# Revit family: APL Residential Thermal Heart Hinged Door Open In
name_source: partatom
category: Doors
revit_build: Autodesk Revit LT 2017 (Build: 20160225_1515(x64)
units: mm (PartAtom-declared; Revit-internal decimal feet)

## family parameters
Always vertical = Yes
Cut with Voids When Loaded = No
Host = Wall
OmniClass Number = 23.30.10.00
OmniClass Title = Doors
Room Calculation Point = No
Shared = No

## types (2) — shared parameters
Analytic Construction = <None>
Frame Projection Int. = 20 mm  [stored 0.0656168 ft]
Frame Width Sill = 15 mm  [stored 0.0492126 ft]
Function = Interior
Groove = 10 mm  [stored 0.0328084 ft]
Height = 2303 mm
Jamb Liner 1 = Yes
Jamb Liner 2 = Yes
Liner End = 10 mm  [stored 0.0328084 ft]
Liner Head = Yes
Liner Sill = No
Panel = 720 mm  [stored 2.3622 ft]
Plan Swing = Yes
Rough Height = 2315 mm  [stored 7.59514 ft]
Rough Width = 815 mm
Wall Closure = By host
Width = 800 mm  [stored 2.62467 ft]

## per-type parameters (varying)
| type | Frame Projection Ext. | Frame Width | Liner | Reveal Liner |
| Architrave | 13 mm | 12 mm  [stored 0.0393701 ft] | 51 mm | No |
| Liner | 14 mm  [stored 0.0459318 ft] | 13 mm | 407 mm | Yes |

type visibility flags (boolean, named after types; folded from table):
- Architrave: Yes: Architrave
- Liner: Yes: (none)

note: [stored X ft] marks values corroborated as IEEE doubles in the binary element streams (Revit-internal decimal feet)

## geometry (parser evidence)
native form markers: Sweep x18
no freeform markers — native parametric forms only
